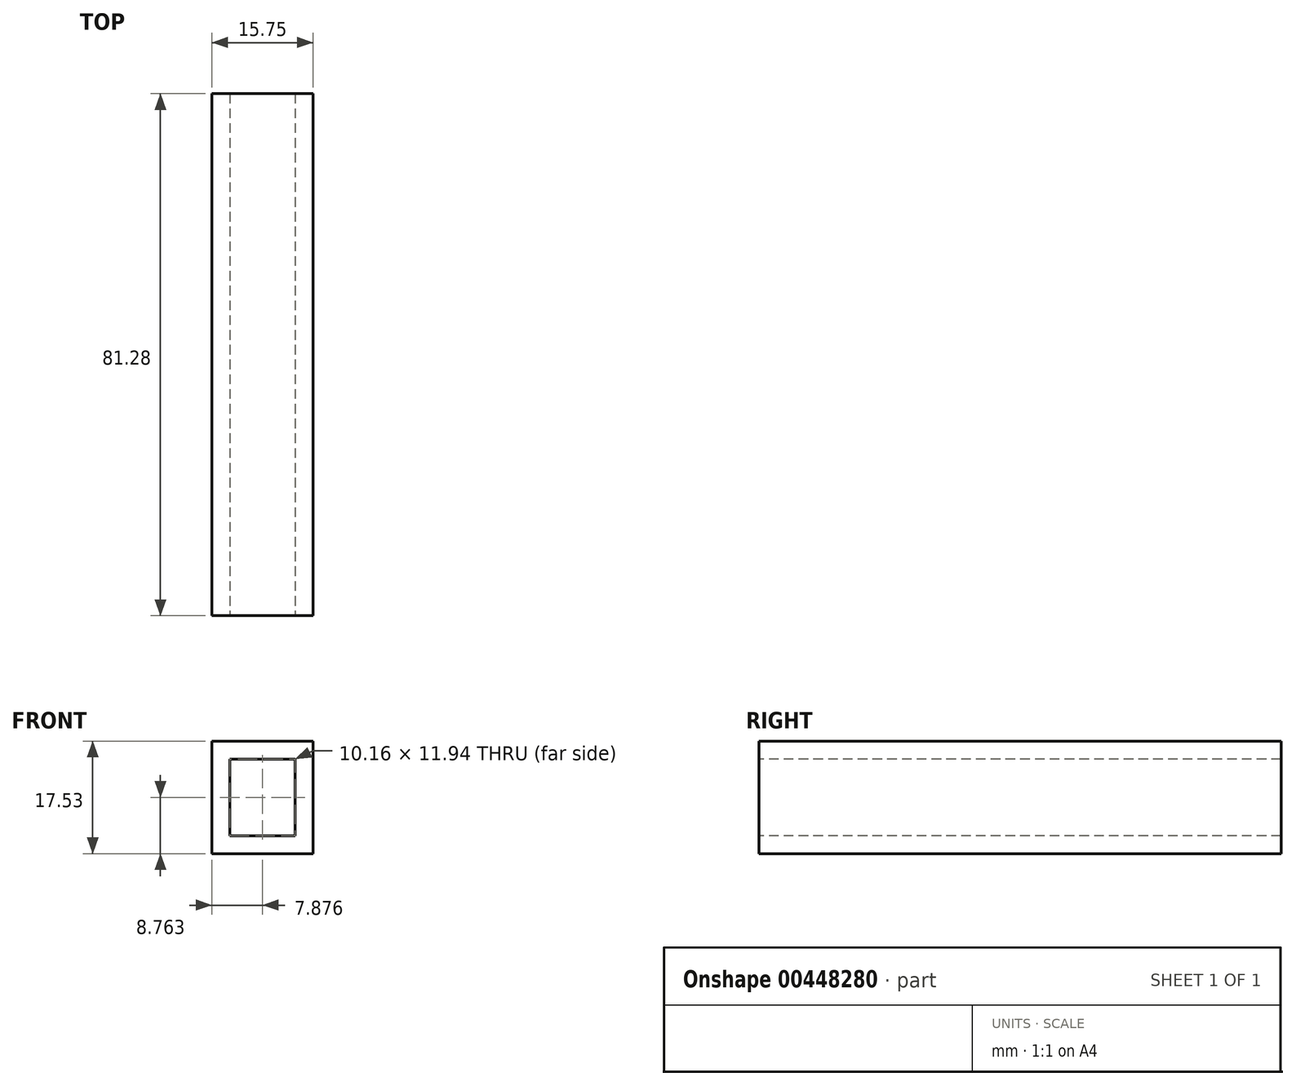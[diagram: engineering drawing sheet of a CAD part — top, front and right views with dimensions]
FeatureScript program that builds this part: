
annotation { "Feature Type Name" : "Feature", "Feature Type Description" : "" }
export const myFeature = defineFeature(function(context is Context, id is Id, definition is map)
    precondition{}
    {
        {
            var Q0;
            Q0=qCreatedBy(makeId("Top.planeOp"),FACE);
            var sketch = newSketch(context, id + "F0", { "sketchPlane" : qUnion([Q0])});
            skLineSegment(sketch, "E0.bottom", {"start": v(-15.75, 43) * mm, "end": v(0, 43) * mm});
            skLineSegment(sketch, "E0.top", {"start": v(-15.75, -38.28) * mm, "end": v(0, -38.28) * mm});
            skLineSegment(sketch, "E0.left", {"start": v(-15.75, 43) * mm, "end": v(-15.75, -38.28) * mm});
            skLineSegment(sketch, "E0.right", {"start": v(0, 43) * mm, "end": v(0, -38.28) * mm});
            skSolve(sketch);
        }
        {
            var Q0;
            Q0 = qSketchRegion(id + "F0", true);
            extrude(context, id + "F1", {"entities" : qUnion([Q0]), "depth" : 17.53 * mm});
        }
        {
            var Q0;
            Q0=makeQuery(id+"F1.opExtrude","SWEPT_FACE",FACE,{"disambiguationData":[OSD([sQuery(id+"F0.wireOp",EDGE,"E0.top")])]});
            var sketch = newSketch(context, id + "F2", { "sketchPlane" : qUnion([Q0])});
            skLineSegment(sketch, "E1.0", {"start": v(-12.95, 2.8) * mm, "end": v(-2.8, 2.8) * mm});
            skLineSegment(sketch, "E1.1", {"start": v(-12.95, 14.73) * mm, "end": v(-12.95, 2.8) * mm});
            skLineSegment(sketch, "E1.2", {"start": v(-2.8, 14.73) * mm, "end": v(-12.95, 14.73) * mm});
            skLineSegment(sketch, "E1.3", {"start": v(-2.8, 2.8) * mm, "end": v(-2.8, 14.73) * mm});
            skSolve(sketch);
        }
        {
            var Q0;
            Q0=makeQuery(id+"F2.imprint","IMPRINT",FACE,{"disambiguationData":[TD([[makeQuery(id+"F2.imprint","IMPRINT",EDGE,{"derivedFrom":sQuery(id+"F2.wireOp",EDGE,"E1.0")}),1.0]])]});
            extrude(context, id + "F3", {"entities" : qUnion([Q0]), "operationType" : NewBodyOperationType.REMOVE, "oppositeDirection" : true, "depth" : 85.34 * mm});
        }
    });
